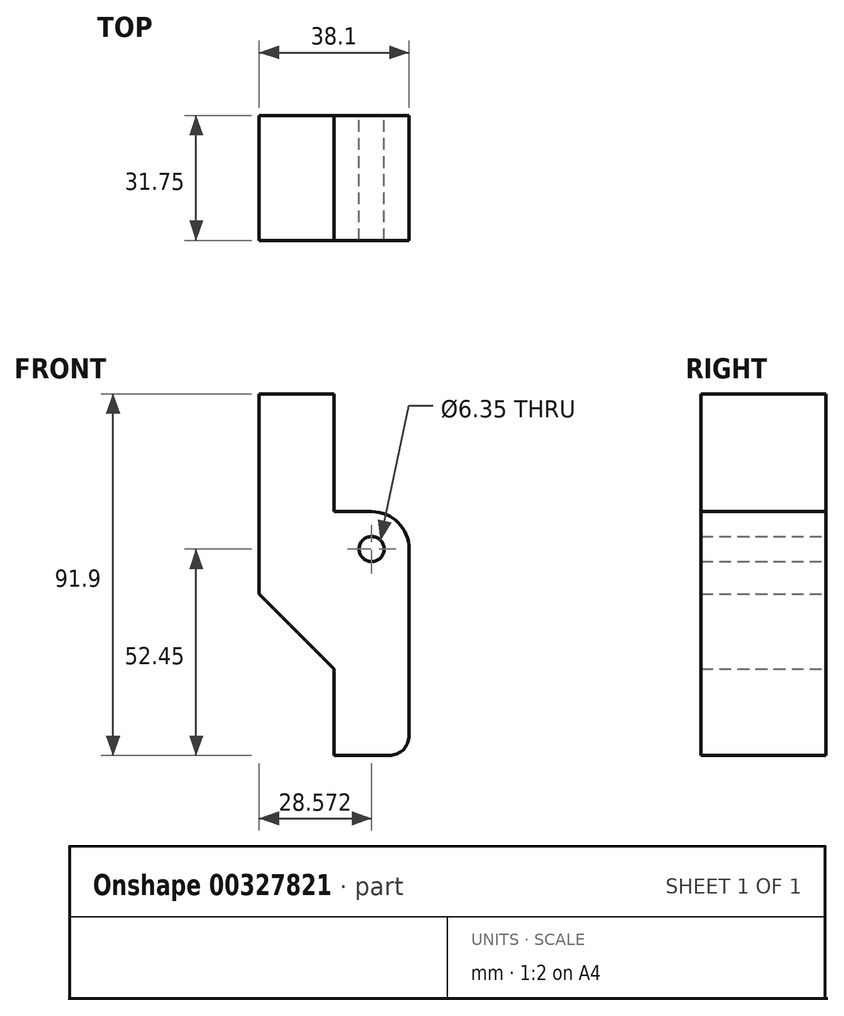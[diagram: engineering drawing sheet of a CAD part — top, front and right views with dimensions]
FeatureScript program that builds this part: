
annotation { "Feature Type Name" : "Feature", "Feature Type Description" : "" }
export const myFeature = defineFeature(function(context is Context, id is Id, definition is map)
    precondition{}
    {
        {
            var Q0;
            Q0=qCreatedBy(makeId("Front.planeOp"),FACE);
            var sketch = newSketch(context, id + "F0", { "sketchPlane" : qUnion([Q0])});
            skLineSegment(sketch, "E0.bottom", {"start": v(-47.01, 29.92) * mm, "end": v(-27.96, 29.92) * mm});
            skLineSegment(sketch, "E0.top", {"start": v(-47.01, -32.05) * mm, "end": v(-27.96, -32.05) * mm});
            skLineSegment(sketch, "E0.left", {"start": v(-47.01, -10) * mm, "end": v(-47.01, -32.05) * mm});
            skLineSegment(sketch, "E0.right", {"start": v(-27.96, 29.92) * mm, "end": v(-27.96, -32.05) * mm});
            skCircle(sketch, "E1", {"center": v(-37.49, 20.4) * mm, "radius": 3.18 * mm});
            skLineSegment(sketch, "E2", {"start": v(-66.06, 9.05) * mm, "end": v(-66.06, 59.85) * mm});
            skLineSegment(sketch, "E3", {"start": v(-66.06, 59.85) * mm, "end": v(-47.01, 59.85) * mm});
            skLineSegment(sketch, "E4", {"start": v(-47.01, 59.85) * mm, "end": v(-47.01, 29.92) * mm});
            skLineSegment(sketch, "E5", {"start": v(-66.06, 9.05) * mm, "end": v(-47.01, -10) * mm});
            skSolve(sketch);
        }
        {
            var Q0;
            Q0 = qSketchRegion(id + "F0", true);
            extrude(context, id + "F1", {"entities" : qUnion([Q0]), "depth" : 31.75 * mm});
        }
        {
            var Q0;
            Q0=makeQuery(id+"F1.opExtrude","SWEPT_EDGE",EDGE,{"disambiguationData":[OSD([sQuery(id+"F0.wireOp",EDGE,"E0.top"),sQuery(id+"F0.wireOp",EDGE,"E0.right")])]});
            fillet(context, id + "F2", {"entities" : qUnion([Q0]), "radius" : 5.08 * mm, "tangentPropagation" : true, "allowEdgeOverflow" : false});
        }
        {
            var Q0;
            Q0=makeQuery(id+"F1.opExtrude","SWEPT_EDGE",EDGE,{"disambiguationData":[OSD([sQuery(id+"F0.wireOp",EDGE,"E0.bottom"),sQuery(id+"F0.wireOp",EDGE,"E0.right")])]});
            fillet(context, id + "F3", {"entities" : qUnion([Q0]), "radius" : 9.52 * mm, "tangentPropagation" : true, "allowEdgeOverflow" : false});
        }
    });
